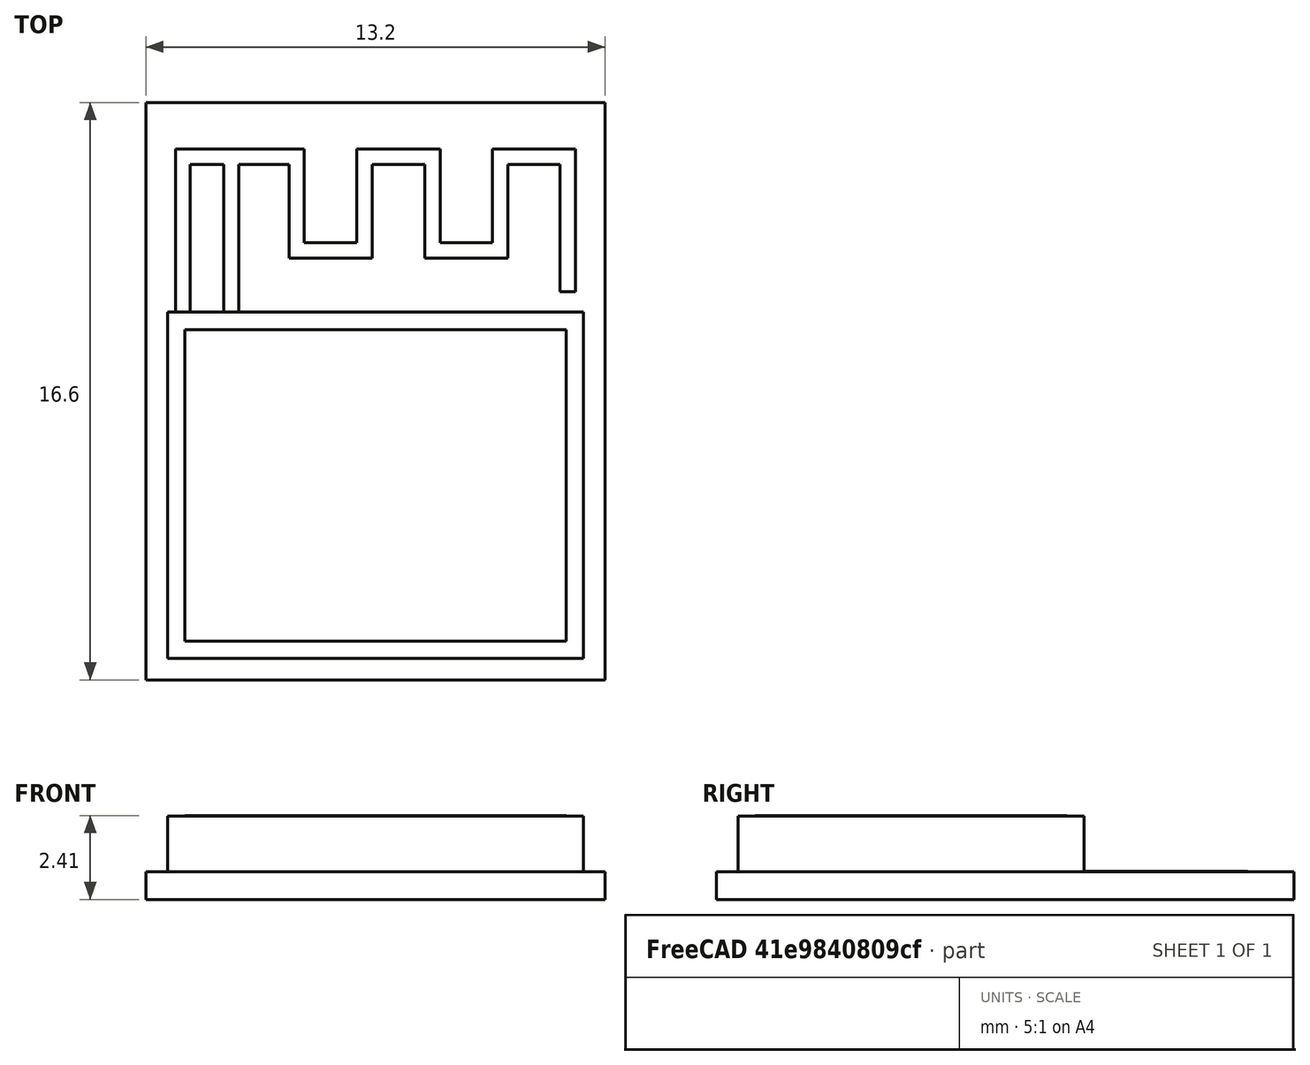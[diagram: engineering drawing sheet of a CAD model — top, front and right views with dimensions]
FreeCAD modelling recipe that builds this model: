
FCSTD DOCUMENT  (FreeCAD 0.18R4 (GitTag))
Label: esp
License: All rights reserved
LicenseURL: http://en.wikipedia.org/wiki/All_rights_reserved
objects: Part::Box×3, Part::Feature×1, Part::Extrusion×1
note: 5 computed .brp shape members not serialized (recipe doc carries the construction recipe); baked Part::Feature solids carry a one-line shape summary decoded from their .brp

FEATURE [Part::Box] Box  label="PCB"
  AttacherType = Attacher::AttachEngine3D
  Height = 0.8
  Length = 13.2
  Width = 16.6
FEATURE [Part::Box] Box001  label="Shield"
  AttacherType = Attacher::AttachEngine3D
  Height = 1.6
  Length = 11.95
  Placement = pos=(0.62,0.62,0.8) rot=(0,0,1;0rad)
  Width = 9.95
FEATURE [Part::Feature] path847
  Placement = pos=(0.85,15.266,0.8) rot=(0,0,1;0rad)
  shape: bbox 11.5 x 4.696 x 2e-07 mm, 1 faces, 0 solids (baked)
FEATURE [Part::Extrusion] Extrude
  Base = -> path847
  Dir = (0,0,1)
  DirMode = 0
  FaceMakerClass = Part::FaceMakerBullseye
  LengthFwd = 0.01
  LengthRev = 0
  Solid = false
  Symmetric = false
FEATURE [Part::Box] Box002  label="Cube"
  AttacherType = Attacher::AttachEngine3D
  Height = 0.01
  Length = 10.95
  Placement = pos=(1.125,1.12,2.4) rot=(0,0,1;0rad)
  Width = 8.95
